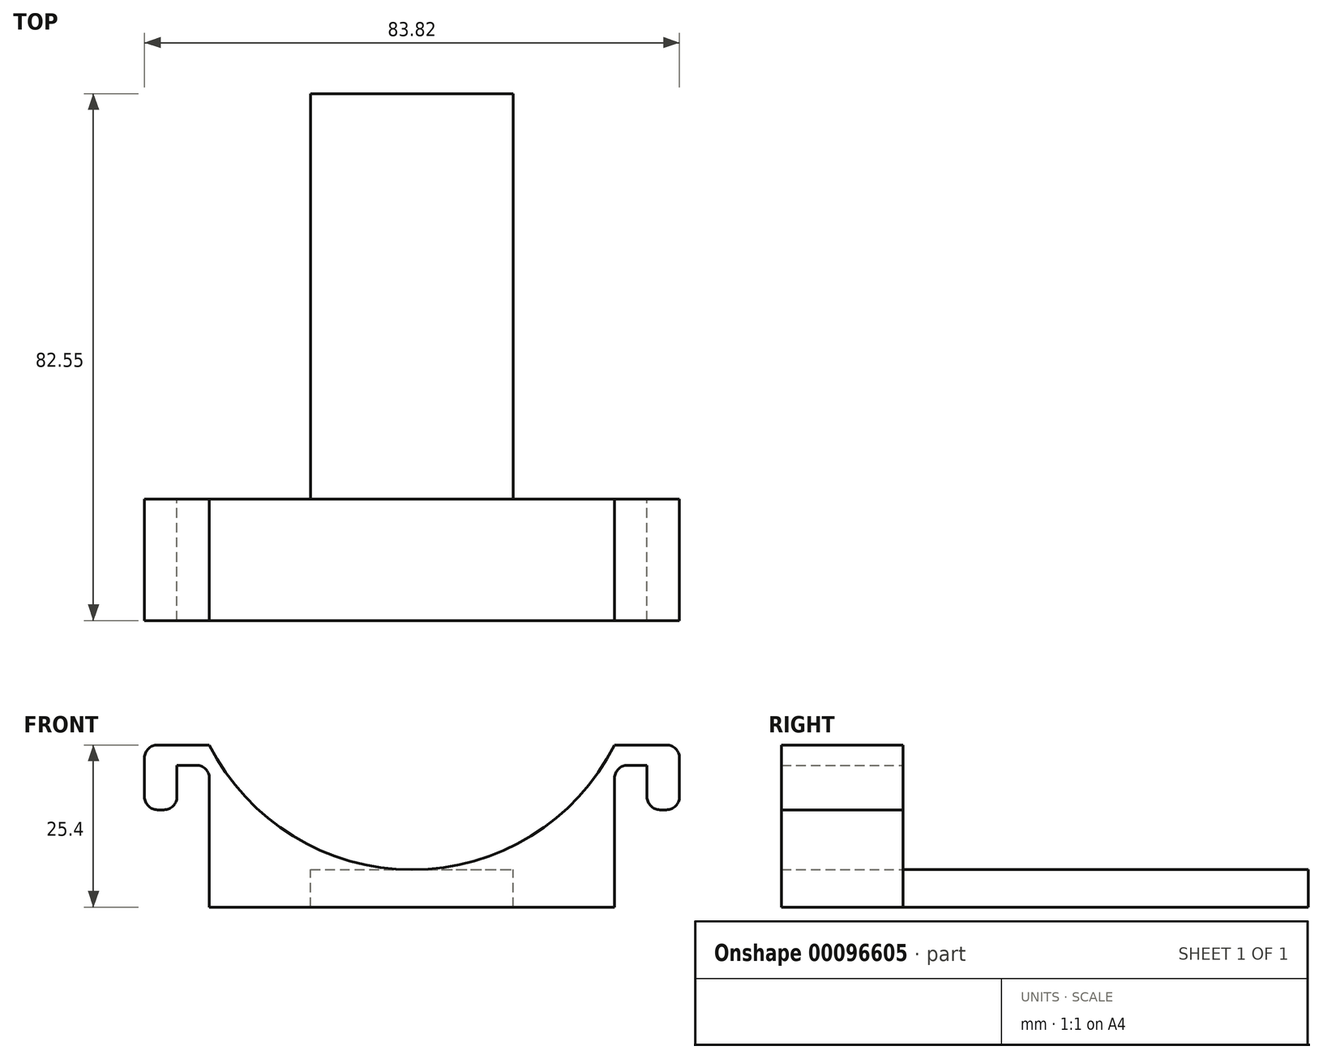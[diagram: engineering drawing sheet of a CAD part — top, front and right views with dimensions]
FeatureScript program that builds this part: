
annotation { "Feature Type Name" : "Feature", "Feature Type Description" : "" }
export const myFeature = defineFeature(function(context is Context, id is Id, definition is map)
    precondition{}
    {
        {
            var Q0;
            Q0=qCreatedBy(makeId("Front.planeOp"),FACE);
            var sketch = newSketch(context, id + "F0", { "sketchPlane" : qUnion([Q0])});
            skLineSegment(sketch, "E0", {"start": v(-31.75, 0) * mm, "end": v(31.75, 0) * mm});
            skPoint(sketch, "E1", {"position": v(0, 0) * mm});
            skArc(sketch, "E2", {"start": v(-31.75, 25.4) * mm, "mid": v(0, 5.85) * mm, "end": v(31.75, 25.4) * mm});
            skLineSegment(sketch, "E3", {"start": v(-31.75, 25.4) * mm, "end": v(-31.75, 0) * mm});
            skLineSegment(sketch, "E4", {"start": v(31.75, 20.2) * mm, "end": v(31.75, 0) * mm});
            skLineSegment(sketch, "E5", {"start": v(31.75, 25.4) * mm, "end": v(39.88, 25.4) * mm});
            skLineSegment(sketch, "E6", {"start": v(41.91, 23.37) * mm, "end": v(41.91, 17.27) * mm});
            skLineSegment(sketch, "E7", {"start": v(39.88, 15.24) * mm, "end": v(38.86, 15.24) * mm});
            skLineSegment(sketch, "E8", {"start": v(36.83, 17.27) * mm, "end": v(36.83, 22.23) * mm});
            skLineSegment(sketch, "E9", {"start": v(36.83, 22.23) * mm, "end": v(33.78, 22.23) * mm});
            skPoint(sketch, "E10.visualSharp", {"position": v(41.91, 25.4) * mm});
            skArc(sketch, "E10.filletArc", {"start": v(41.91, 23.37) * mm, "mid": v(41.31, 24.8) * mm, "end": v(39.88, 25.4) * mm});
            skPoint(sketch, "E11.visualSharp", {"position": v(36.83, 15.24) * mm});
            skArc(sketch, "E11.filletArc", {"start": v(36.83, 17.27) * mm, "mid": v(37.43, 15.84) * mm, "end": v(38.86, 15.24) * mm});
            skPoint(sketch, "E12.visualSharp", {"position": v(41.91, 15.24) * mm});
            skArc(sketch, "E12.filletArc", {"start": v(39.88, 15.24) * mm, "mid": v(41.31, 15.84) * mm, "end": v(41.91, 17.27) * mm});
            skLineSegment(sketch, "E13", {"start": v(0, 0) * mm, "end": v(0, 5.85) * mm});
            skPoint(sketch, "E14.newPointA", {"position": v(31.75, 25.4) * mm});
            skPoint(sketch, "E14.newPointB", {"position": v(31.75, 22.22) * mm});
            skArc(sketch, "E14.filletArc", {"start": v(33.78, 22.23) * mm, "mid": v(32.35, 21.63) * mm, "end": v(31.75, 20.2) * mm});
            skSolve(sketch);
        }
        {
            var Q0;
            {var subQ4=sQuery(id+"F0.wireOp",EDGE,"E13");Q0=makeQuery(id+"F0.imprint","IMPRINT",FACE,{"disambiguationData":[TD([[makeQuery(id+"F0.imprint","IMPRINT",EDGE,{"derivedFrom":subQ4}),-1.0]])]});}
            var Q1;
            {var subQ0=sQuery(id+"F0.wireOp",EDGE,"E5");Q1=makeQuery(id+"F0.imprint","IMPRINT",FACE,{"disambiguationData":[TD([[makeQuery(id+"F0.imprint","IMPRINT",EDGE,{"derivedFrom":subQ0}),-1.0]])]});}
            extrude(context, id + "F1", {"entities" : qUnion([Q0, Q1]), "depth" : 19.05 * mm, "offsetDistance" : 25.4 * mm});
        }
        {
            var Q0;
            Q0=makeQuery(id+"F1.opExtrude","SWEPT_BODY",BODY,{"disambiguationData":[OSD([sQuery(id+"F0.wireOp",EDGE,"E0"),sQuery(id+"F0.wireOp",EDGE,"E2"),sQuery(id+"F0.wireOp",EDGE,"E4"),sQuery(id+"F0.wireOp",EDGE,"E5"),sQuery(id+"F0.wireOp",EDGE,"E6"),sQuery(id+"F0.wireOp",EDGE,"E7"),sQuery(id+"F0.wireOp",EDGE,"E8"),sQuery(id+"F0.wireOp",EDGE,"E9"),sQuery(id+"F0.wireOp",EDGE,"E10.filletArc"),sQuery(id+"F0.wireOp",EDGE,"E11.filletArc"),sQuery(id+"F0.wireOp",EDGE,"E12.filletArc"),sQuery(id+"F0.wireOp",EDGE,"E13"),sQuery(id+"F0.wireOp",EDGE,"E14.filletArc")])]});
            var Q1;
            Q1=qCreatedBy(makeId("Right.planeOp"),FACE);
            mirror(context, id + "F2", {"operationType" : NewBodyOperationType.ADD, "entities" : qUnion([Q0]), "mirrorPlane" : qUnion([Q1])});
        }
        {
            var Q0;
            Q0=qCreatedBy(makeId("Front.planeOp"),FACE);
            var sketch = newSketch(context, id + "F3", { "sketchPlane" : qUnion([Q0])});
            skLineSegment(sketch, "E15", {"start": v(-15.87, 0) * mm, "end": v(15.87, 0) * mm});
            skPoint(sketch, "E16", {"position": v(0, 0) * mm});
            skLineSegment(sketch, "E17", {"start": v(-15.87, 0) * mm, "end": v(-15.87, 5.85) * mm});
            skLineSegment(sketch, "E18", {"start": v(-15.88, 5.85) * mm, "end": v(15.88, 5.85) * mm});
            skLineSegment(sketch, "E19", {"start": v(15.87, 0) * mm, "end": v(15.87, 5.85) * mm});
            skSolve(sketch);
        }
        {
            var Q0;
            Q0 = qSketchRegion(id + "F3", true);
            extrude(context, id + "F4", {"entities" : qUnion([Q0]), "operationType" : NewBodyOperationType.ADD, "oppositeDirection" : true, "depth" : 63.5 * mm, "offsetDistance" : 25.4 * mm});
        }
    });
